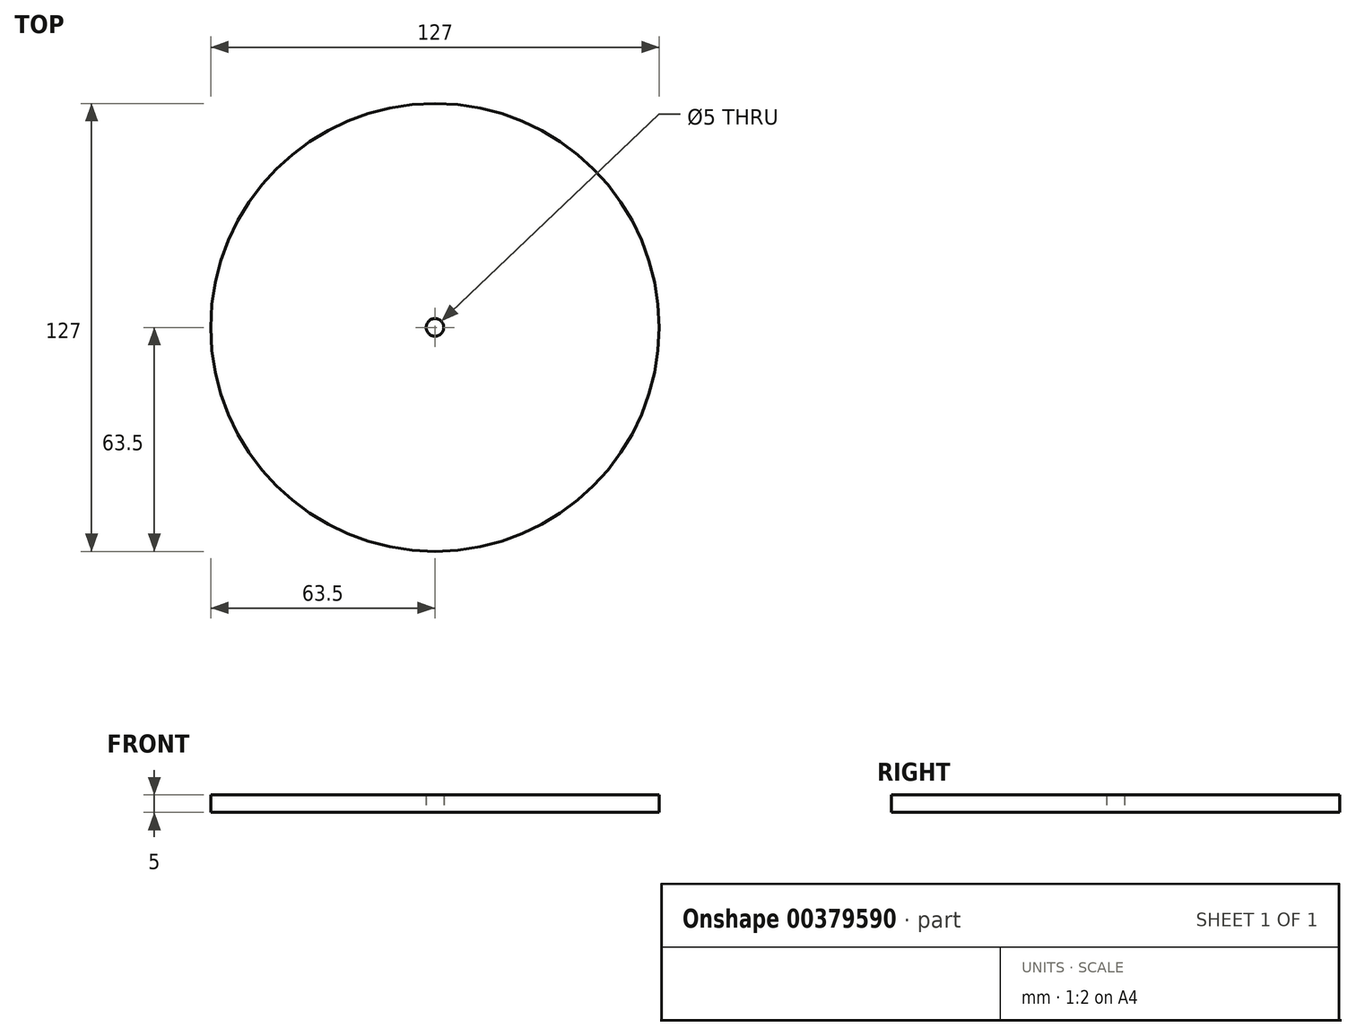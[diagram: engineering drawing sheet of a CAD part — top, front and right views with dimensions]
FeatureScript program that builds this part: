
annotation { "Feature Type Name" : "Feature", "Feature Type Description" : "" }
export const myFeature = defineFeature(function(context is Context, id is Id, definition is map)
    precondition{}
    {
        {
            var Q0;
            Q0=qCreatedBy(makeId("Top.planeOp"),FACE);
            var sketch = newSketch(context, id + "F0", { "sketchPlane" : qUnion([Q0])});
            skCircle(sketch, "E0", {"center": v(0, 0) * mm, "radius": 2.5 * mm});
            skCircle(sketch, "E1", {"center": v(0, 0) * mm, "radius": 63.5 * mm});
            skSolve(sketch);
        }
        {
            var Q0;
            Q0 = qSketchRegion(id + "F0", true);
            extrude(context, id + "F1", {"entities" : qUnion([Q0]), "depth" : 5 * mm});
        }
    });
